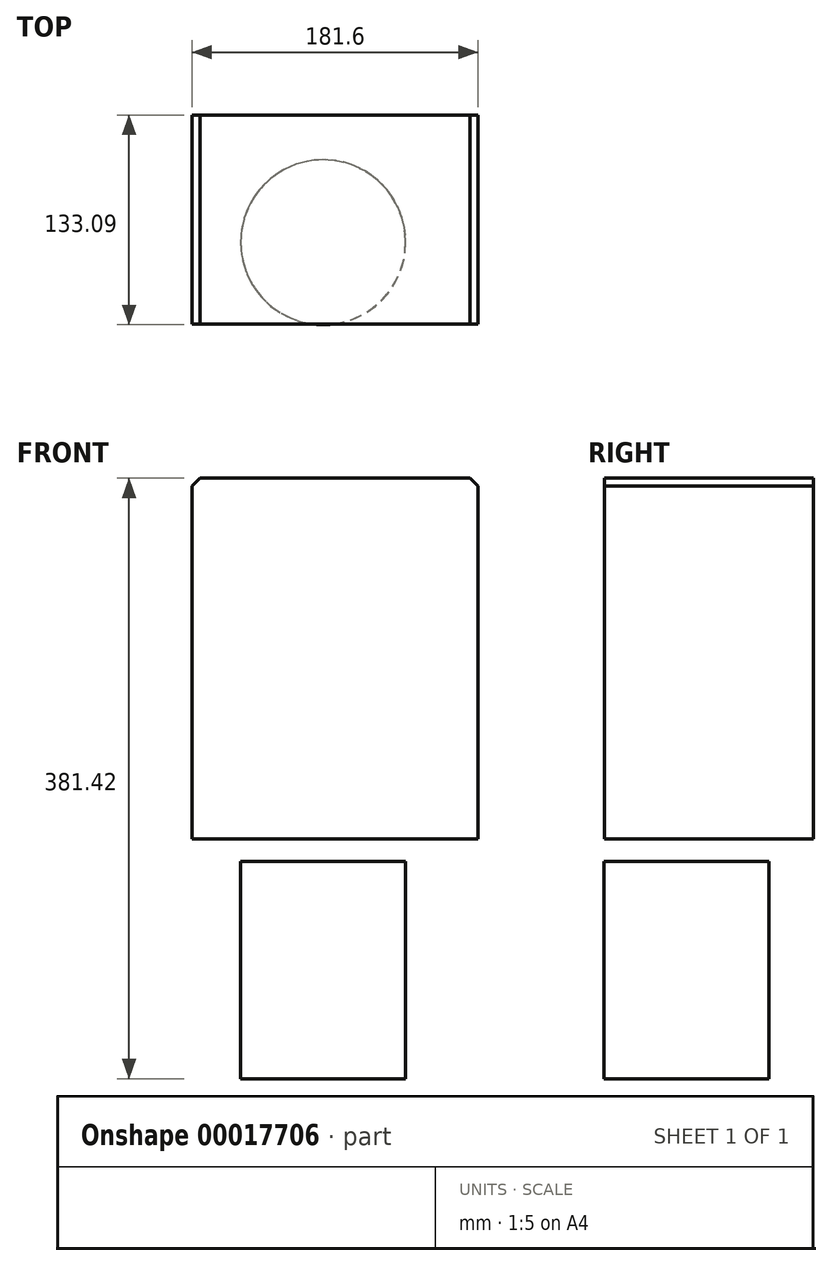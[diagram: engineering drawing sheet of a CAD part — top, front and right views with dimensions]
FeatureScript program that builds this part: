
annotation { "Feature Type Name" : "Feature", "Feature Type Description" : "" }
export const myFeature = defineFeature(function(context is Context, id is Id, definition is map)
    precondition{}
    {
        {
            var Q0;
            Q0=qCreatedBy(makeId("Front.planeOp"),FACE);
            var sketch = newSketch(context, id + "F7", { "sketchPlane" : qUnion([Q0])});
            skLineSegment(sketch, "E0.bottom", {"start": v(-39.68, 39.38) * mm, "end": v(26.98, 39.38) * mm});
            skLineSegment(sketch, "E0.top", {"start": v(-39.68, -52.78) * mm, "end": v(26.98, -52.78) * mm});
            skLineSegment(sketch, "E0.left", {"start": v(-39.68, 39.38) * mm, "end": v(-39.68, -52.78) * mm});
            skLineSegment(sketch, "E0.right", {"start": v(26.98, 39.38) * mm, "end": v(26.98, -52.78) * mm});
            skSolve(sketch);
        }
        {
            var Q0;
            Q0=sQuery(id+"F7.wireOp",EDGE,"E0.right");
            extrude(context, id + "F8", {"bodyType" : ToolBodyType.SURFACE, "surfaceEntities" : qUnion([Q0]), "depth" : 25.4 * mm});
        }
        {
            var Q0;
            Q0=makeQuery(id+"F8.opExtrude","SWEPT_BODY",BODY,{"disambiguationData":[OSD([sQuery(id+"F7.wireOp",EDGE,"E0.right")])]});
            deleteBodies(context, id + "F9", {"entities" : qUnion([Q0])});
        }
        {
            var Q0;
            Q0=qCreatedBy(makeId("Front.planeOp"),FACE);
            var sketch = newSketch(context, id + "F10", { "sketchPlane" : qUnion([Q0])});
            skLineSegment(sketch, "E1.bottom", {"start": v(55.69, 61.16) * mm, "end": v(-125.91, 61.16) * mm});
            skLineSegment(sketch, "E1.top", {"start": v(55.69, -167.86) * mm, "end": v(-125.91, -167.86) * mm});
            skLineSegment(sketch, "E1.left", {"start": v(55.69, 61.16) * mm, "end": v(55.69, -167.86) * mm});
            skLineSegment(sketch, "E1.right", {"start": v(-125.91, 61.16) * mm, "end": v(-125.91, -167.86) * mm});
            skSolve(sketch);
        }
        {
            var Q0;
            Q0=makeQuery(id+"F10.imprint","IMPRINT",FACE,{"disambiguationData":[TD([[makeQuery(id+"F10.imprint","IMPRINT",EDGE,{"derivedFrom":sQuery(id+"F10.wireOp",EDGE,"E1.bottom")}),1.0]])]});
            extrude(context, id + "F0", {"entities" : qUnion([Q0]), "oppositeDirection" : true, "depth" : 124.2 * mm});
        }
        {
            var Q0;
            Q0=makeQuery(id+"F0.opExtrude","SWEPT_EDGE",EDGE,{"disambiguationData":[OSD([sQuery(id+"F10.wireOp",EDGE,"E1.bottom"),sQuery(id+"F10.wireOp",EDGE,"E1.left")])]});
            var Q1;
            Q1=makeQuery(id+"F0.opExtrude","SWEPT_EDGE",EDGE,{"disambiguationData":[OSD([sQuery(id+"F10.wireOp",EDGE,"E1.bottom"),sQuery(id+"F10.wireOp",EDGE,"E1.right")])]});
            chamfer(context, id + "F1", {"entities" : qUnion([Q0, Q1]), "width" : 5.08 * mm, "tangentPropagation" : true});
        }
        {
            var Q0;
            Q0=makeQuery(id+"F0.opExtrude","SWEPT_FACE",FACE,{"disambiguationData":[OSD([sQuery(id+"F10.wireOp",EDGE,"E1.top")])]});
            cPlane(context, id + "F2", {"entities" : qUnion([Q0]), "cplaneType" : CPlaneType.OFFSET, "offset" : 152.4 * mm, "width" : 152.4 * mm, "height" : 152.4 * mm});
        }
        {
            var Q0;
            Q0=qCreatedBy(id+"F2.planeOp",FACE);
            var sketch = newSketch(context, id + "F3", { "sketchPlane" : qUnion([Q0])});
            skCircle(sketch, "E2", {"center": v(-42.62, -51.99) * mm, "radius": 52.37 * mm});
            skSolve(sketch);
        }
        {
            var Q0;
            Q0=makeQuery(id+"F3.imprint","IMPRINT",FACE,{"disambiguationData":[TD([[makeQuery(id+"F3.imprint","IMPRINT",EDGE,{"derivedFrom":sQuery(id+"F3.wireOp",EDGE,"E2")}),1.0]])]});
            extrude(context, id + "F4", {"entities" : qUnion([Q0]), "oppositeDirection" : true, "depth" : 137.87 * mm});
        }
        {
            var Q0;
            Q0=makeQuery(id+"F0.opExtrude","CAP_FACE",FACE,{"disambiguationData":[OSD([sQuery(id+"F10.wireOp",EDGE,"E1.bottom"),sQuery(id+"F10.wireOp",EDGE,"E1.top"),sQuery(id+"F10.wireOp",EDGE,"E1.left"),sQuery(id+"F10.wireOp",EDGE,"E1.right")])],"isStart":false});
            var sketch = newSketch(context, id + "F5", { "sketchPlane" : qUnion([Q0])});
            skLineSegment(sketch, "E3.bottom", {"start": v(43.05, -67.5) * mm, "end": v(0, -67.5) * mm});
            skLineSegment(sketch, "E3.top", {"start": v(43.05, -131.85) * mm, "end": v(0, -131.85) * mm});
            skLineSegment(sketch, "E3.left", {"start": v(43.05, -67.5) * mm, "end": v(43.05, -131.85) * mm});
            skLineSegment(sketch, "E3.right", {"start": v(0, -67.5) * mm, "end": v(0, -131.85) * mm});
            skLineSegment(sketch, "E4.bottom", {"start": v(-3.14, -58.81) * mm, "end": v(77.75, -58.81) * mm});
            skLineSegment(sketch, "E4.top", {"start": v(-3.14, 0) * mm, "end": v(77.75, 0) * mm});
            skLineSegment(sketch, "E4.left", {"start": v(-3.14, -58.81) * mm, "end": v(-3.14, 0) * mm});
            skLineSegment(sketch, "E4.right", {"start": v(77.75, -58.81) * mm, "end": v(77.75, 0) * mm});
            skSolve(sketch);
        }
        {
            var Q0;
            Q0 = qSketchRegion(id + "F5", true);
            var Q1;
            Q1=makeQuery(id+"F5.imprint","IMPRINT",FACE,{"disambiguationData":[TD([[makeQuery(id+"F5.imprint","IMPRINT",EDGE,{"derivedFrom":sQuery(id+"F5.wireOp",EDGE,"E3.bottom")}),-1.0]])]});
            extrude(context, id + "F6", {"entities" : qUnion([Q0, Q1]), "operationType" : NewBodyOperationType.ADD, "depth" : 8.5 * mm});
        }
    });
